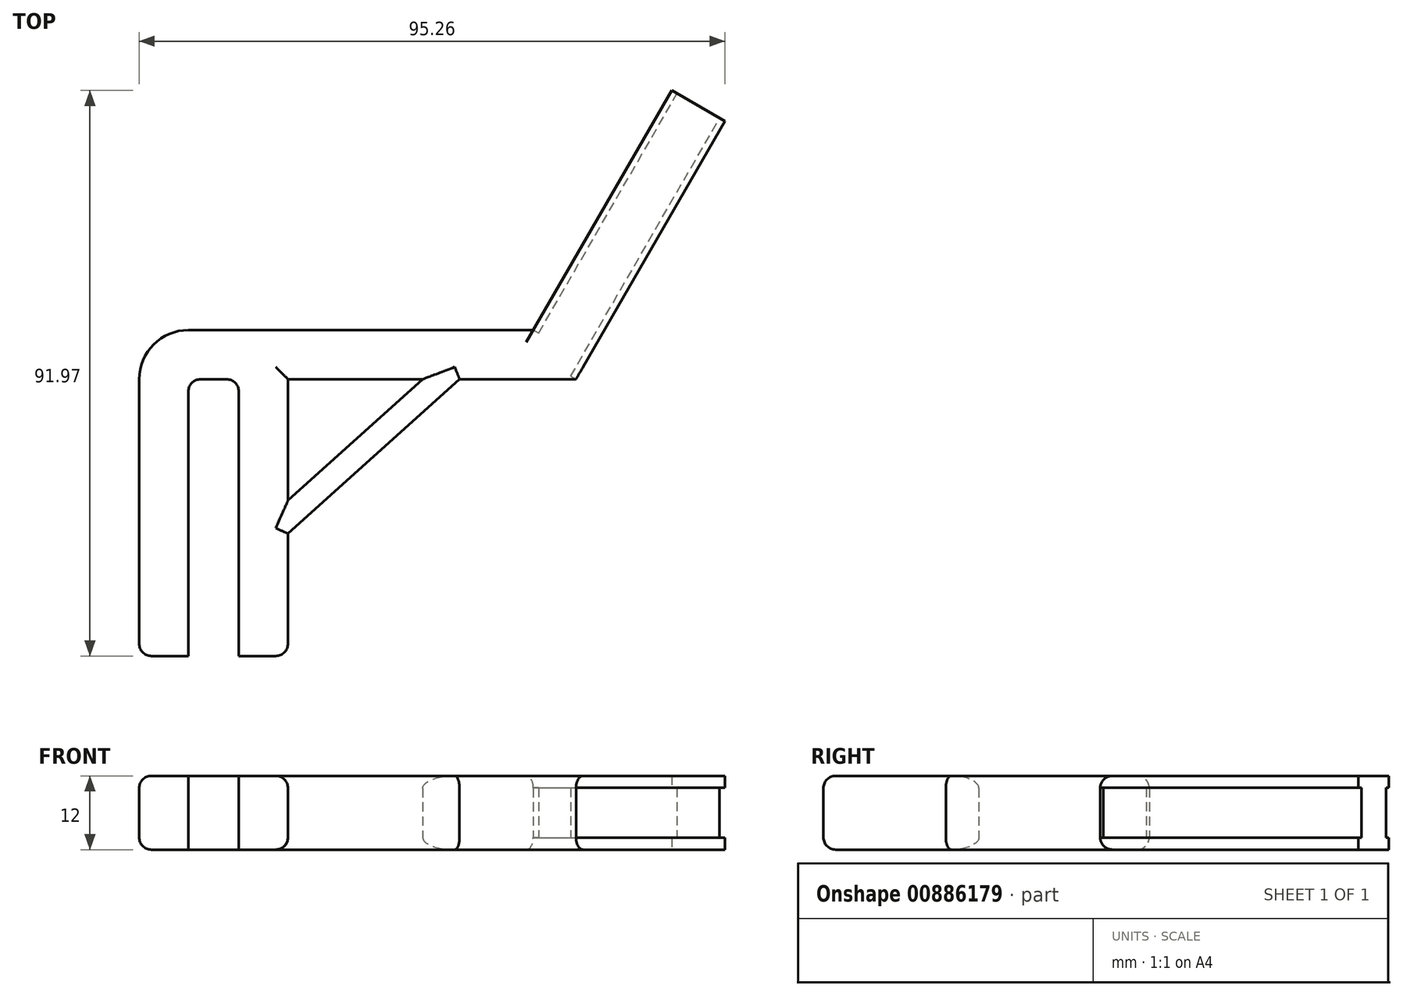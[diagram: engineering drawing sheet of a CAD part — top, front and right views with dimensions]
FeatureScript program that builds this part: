
annotation { "Feature Type Name" : "Feature", "Feature Type Description" : "" }
export const myFeature = defineFeature(function(context is Context, id is Id, definition is map)
    precondition{}
    {
        {
            var Q0;
            Q0=qCreatedBy(makeId("Top.planeOp"),FACE);
            var sketch = newSketch(context, id + "F0", { "sketchPlane" : qUnion([Q0])});
            skLineSegment(sketch, "E0", {"start": v(0, 0) * mm, "end": v(0, 45) * mm});
            skLineSegment(sketch, "E1", {"start": v(24.2, 45) * mm, "end": v(24.2, 25.28) * mm});
            skLineSegment(sketch, "E2", {"start": v(24.2, 0) * mm, "end": v(16.2, 0) * mm});
            skLineSegment(sketch, "E3", {"start": v(16.2, 0) * mm, "end": v(16.2, 43) * mm});
            skLineSegment(sketch, "E4", {"start": v(14.2, 45) * mm, "end": v(10, 45) * mm});
            skLineSegment(sketch, "E5", {"start": v(8, 43) * mm, "end": v(8, 0) * mm});
            skLineSegment(sketch, "E6", {"start": v(8, 0) * mm, "end": v(0, 0) * mm});
            skLineSegment(sketch, "E7", {"start": v(24.2, 45) * mm, "end": v(46.11, 45) * mm});
            skLineSegment(sketch, "E8", {"start": v(71.03, 45) * mm, "end": v(95.26, 86.97) * mm});
            skLineSegment(sketch, "E9", {"start": v(95.26, 86.97) * mm, "end": v(86.6, 91.97) * mm});
            skLineSegment(sketch, "E10", {"start": v(64.1, 53) * mm, "end": v(8, 53) * mm});
            skLineSegment(sketch, "E11", {"start": v(86.6, 91.97) * mm, "end": v(64.1, 53) * mm});
            skLineSegment(sketch, "E12.0.left", {"start": v(24.2, 25.28) * mm, "end": v(46.11, 45) * mm});
            skLineSegment(sketch, "E12.0.right", {"start": v(24.2, 19.9) * mm, "end": v(52.09, 45) * mm});
            skLineSegment(sketch, "E13.trimOffspring", {"start": v(52.09, 45) * mm, "end": v(71.03, 45) * mm});
            skLineSegment(sketch, "E14.trimOffspring", {"start": v(24.2, 19.9) * mm, "end": v(24.2, 0) * mm});
            skPoint(sketch, "E15.visualSharp", {"position": v(0, 53) * mm});
            skPoint(sketch, "E16.visualSharp", {"position": v(16.2, 45) * mm});
            skArc(sketch, "E16.filletArc", {"start": v(16.2, 43) * mm, "mid": v(15.61, 44.41) * mm, "end": v(14.2, 45) * mm});
            skPoint(sketch, "E17.visualSharp", {"position": v(8, 45) * mm});
            skArc(sketch, "E17.filletArc", {"start": v(10, 45) * mm, "mid": v(8.59, 44.41) * mm, "end": v(8, 43) * mm});
            skArc(sketch, "E18.filletArc", {"start": v(8, 53) * mm, "mid": v(2.34, 50.66) * mm, "end": v(0, 45) * mm});
            skSolve(sketch);
        }
        {
            var Q0;
            Q0=makeQuery(id+"F0.imprint","IMPRINT",FACE,{"disambiguationData":[TD([[makeQuery(id+"F0.imprint","IMPRINT",EDGE,{"derivedFrom":sQuery(id+"F0.wireOp",EDGE,"E0")}),-1.0]])]});
            extrude(context, id + "F1", {"entities" : qUnion([Q0]), "depth" : 12 * mm, "offsetDistance" : 25 * mm});
        }
        {
            var Q0;
            Q0=makeQuery(id+"F1.opExtrude","SWEPT_FACE",FACE,{"disambiguationData":[OSD([sQuery(id+"F0.wireOp",EDGE,"0EtChF5o-fKpo-bCFs-vnvd-GfJutQpqdpGe"),sQuery(id+"F0.wireOp",EDGE,"E8")])]});
            var sketch = newSketch(context, id + "F2", { "sketchPlane" : qUnion([Q0])});
            skLineSegment(sketch, "E19.bottom", {"start": v(74.49, 10.05) * mm, "end": v(122.95, 10.05) * mm});
            skLineSegment(sketch, "E19.top", {"start": v(74.49, 1.95) * mm, "end": v(122.95, 1.95) * mm});
            skLineSegment(sketch, "E19.left", {"start": v(74.49, 10.05) * mm, "end": v(74.49, 1.95) * mm});
            skLineSegment(sketch, "E19.right", {"start": v(122.95, 10.05) * mm, "end": v(122.95, 1.95) * mm});
            skSolve(sketch);
        }
        {
            var Q0;
            Q0=makeQuery(id+"F2.imprint","IMPRINT",FACE,{"disambiguationData":[TD([[makeQuery(id+"F2.imprint","IMPRINT",EDGE,{"derivedFrom":sQuery(id+"F2.wireOp",EDGE,"E19.bottom")}),-1.0]])]});
            extrude(context, id + "F3", {"entities" : qUnion([Q0]), "operationType" : NewBodyOperationType.REMOVE, "oppositeDirection" : true, "depth" : 1 * mm, "offsetDistance" : 25 * mm});
        }
        {
            var Q0;
            Q0=makeQuery(id+"F1.opExtrude","SWEPT_FACE",FACE,{"disambiguationData":[OSD([sQuery(id+"F0.wireOp",EDGE,"E11")])]});
            var sketch = newSketch(context, id + "F4", { "sketchPlane" : qUnion([Q0])});
            skLineSegment(sketch, "E20.0", {"start": v(-122.95, 12) * mm, "end": v(-77.95, 12) * mm, "construction": true});
            skLineSegment(sketch, "E20.1", {"start": v(-122.95, 12) * mm, "end": v(-122.95, 0) * mm, "construction": true});
            skLineSegment(sketch, "E20.2", {"start": v(-77.95, 12) * mm, "end": v(-77.95, 0) * mm, "construction": true});
            skLineSegment(sketch, "E20.3", {"start": v(-122.95, 0) * mm, "end": v(-77.95, 0) * mm, "construction": true});
            skLineSegment(sketch, "E21.bottom", {"start": v(-77.95, 1.95) * mm, "end": v(-122.95, 1.95) * mm});
            skLineSegment(sketch, "E21.top", {"start": v(-77.95, 10.05) * mm, "end": v(-122.95, 10.05) * mm});
            skLineSegment(sketch, "E21.left", {"start": v(-77.95, 1.95) * mm, "end": v(-77.95, 10.05) * mm});
            skLineSegment(sketch, "E21.right", {"start": v(-122.95, 1.95) * mm, "end": v(-122.95, 10.05) * mm});
            skPoint(sketch, "E21.middle", {"position": v(-100.45, 6) * mm});
            skPoint(sketch, "E21.middle.positionSnap0", {"position": v(-100.45, 0) * mm});
            skPoint(sketch, "E21.middle.positionSnap1", {"position": v(-122.95, 6) * mm});
            skPoint(sketch, "E21.centerSnap0", {"position": v(-100.45, 0) * mm});
            skPoint(sketch, "E21.centerSnap1", {"position": v(-122.95, 6) * mm});
            skSolve(sketch);
        }
        {
            var Q0;
            Q0=makeQuery(id+"F4.imprint","IMPRINT",FACE,{"disambiguationData":[TD([[makeQuery(id+"F4.imprint","IMPRINT",EDGE,{"derivedFrom":sQuery(id+"F4.wireOp",EDGE,"E21.bottom")}),-1.0]])]});
            extrude(context, id + "F5", {"entities" : qUnion([Q0]), "operationType" : NewBodyOperationType.REMOVE, "oppositeDirection" : true, "depth" : 1 * mm, "offsetDistance" : 25 * mm});
        }
        {
            var Q0;
            Q0=makeQuery(id+"F1.opExtrude","CAP_EDGE",EDGE,{"disambiguationData":[OSD([sQuery(id+"F0.wireOp",EDGE,"E12.0.right")])],"isStart":false});
            var Q1;
            Q1=makeQuery(id+"F1.opExtrude","CAP_EDGE",EDGE,{"disambiguationData":[OSD([sQuery(id+"F0.wireOp",EDGE,"E7")])],"isStart":false});
            var Q2;
            Q2=makeQuery(id+"F1.opExtrude","CAP_EDGE",EDGE,{"disambiguationData":[OSD([sQuery(id+"F0.wireOp",EDGE,"E1")])],"isStart":false});
            var Q3;
            Q3=makeQuery(id+"F1.opExtrude","CAP_EDGE",EDGE,{"disambiguationData":[OSD([sQuery(id+"F0.wireOp",EDGE,"E12.0.left")])],"isStart":false});
            var Q4;
            Q4=makeQuery(id+"F1.opExtrude","CAP_EDGE",EDGE,{"disambiguationData":[OSD([sQuery(id+"F0.wireOp",EDGE,"E13.trimOffspring")])],"isStart":false});
            var Q5;
            Q5=makeQuery(id+"F1.opExtrude","CAP_EDGE",EDGE,{"disambiguationData":[OSD([sQuery(id+"F0.wireOp",EDGE,"E14.trimOffspring")])],"isStart":false});
            var Q6;
            Q6=makeQuery(id+"F1.opExtrude","CAP_EDGE",EDGE,{"disambiguationData":[OSD([sQuery(id+"F0.wireOp",EDGE,"E2")])],"isStart":false});
            var Q7;
            Q7=makeQuery(id+"F1.opExtrude","CAP_EDGE",EDGE,{"disambiguationData":[OSD([sQuery(id+"F0.wireOp",EDGE,"E6")])],"isStart":false});
            var Q8;
            Q8=makeQuery(id+"F1.opExtrude","CAP_EDGE",EDGE,{"disambiguationData":[OSD([sQuery(id+"F0.wireOp",EDGE,"E10")])],"isStart":false});
            var Q9;
            Q9=makeQuery(id+"F1.opExtrude","CAP_EDGE",EDGE,{"disambiguationData":[OSD([sQuery(id+"F0.wireOp",EDGE,"E0")])],"isStart":false});
            var Q10;
            Q10=makeQuery(id+"F1.opExtrude","SWEPT_EDGE",EDGE,{"disambiguationData":[OSD([sQuery(id+"F0.wireOp",EDGE,"E2"),sQuery(id+"F0.wireOp",EDGE,"E14.trimOffspring")])]});
            var Q11;
            Q11=makeQuery(id+"F1.opExtrude","SWEPT_EDGE",EDGE,{"disambiguationData":[OSD([sQuery(id+"F0.wireOp",EDGE,"E0"),sQuery(id+"F0.wireOp",EDGE,"E6")])]});
            var Q12;
            Q12=makeQuery(id+"F1.opExtrude","CAP_EDGE",EDGE,{"disambiguationData":[OSD([sQuery(id+"F0.wireOp",EDGE,"E2")])],"isStart":true});
            var Q13;
            Q13=makeQuery(id+"F1.opExtrude","CAP_EDGE",EDGE,{"disambiguationData":[OSD([sQuery(id+"F0.wireOp",EDGE,"E14.trimOffspring")])],"isStart":true});
            var Q14;
            Q14=makeQuery(id+"F1.opExtrude","CAP_EDGE",EDGE,{"disambiguationData":[OSD([sQuery(id+"F0.wireOp",EDGE,"E12.0.right")])],"isStart":true});
            var Q15;
            Q15=makeQuery(id+"F1.opExtrude","CAP_EDGE",EDGE,{"disambiguationData":[OSD([sQuery(id+"F0.wireOp",EDGE,"E13.trimOffspring")])],"isStart":true});
            var Q16;
            Q16=makeQuery(id+"F1.opExtrude","CAP_EDGE",EDGE,{"disambiguationData":[OSD([sQuery(id+"F0.wireOp",EDGE,"E12.0.left")])],"isStart":true});
            var Q17;
            Q17=makeQuery(id+"F1.opExtrude","CAP_EDGE",EDGE,{"disambiguationData":[OSD([sQuery(id+"F0.wireOp",EDGE,"E7")])],"isStart":true});
            var Q18;
            Q18=makeQuery(id+"F1.opExtrude","CAP_EDGE",EDGE,{"disambiguationData":[OSD([sQuery(id+"F0.wireOp",EDGE,"E1")])],"isStart":true});
            var Q19;
            Q19=makeQuery(id+"F1.opExtrude","CAP_EDGE",EDGE,{"disambiguationData":[OSD([sQuery(id+"F0.wireOp",EDGE,"E0")])],"isStart":true});
            var Q20;
            Q20=makeQuery(id+"F1.opExtrude","CAP_EDGE",EDGE,{"disambiguationData":[OSD([sQuery(id+"F0.wireOp",EDGE,"E10")])],"isStart":true});
            var Q21;
            Q21=makeQuery(id+"F1.opExtrude","CAP_EDGE",EDGE,{"disambiguationData":[OSD([sQuery(id+"F0.wireOp",EDGE,"E6")])],"isStart":true});
            fillet(context, id + "F6", {"entities" : qUnion([Q0, Q1, Q2, Q3, Q4, Q5, Q6, Q7, Q8, Q9, Q10, Q11, Q12, Q13, Q14, Q15, Q16, Q17, Q18, Q19, Q20, Q21]), "radius" : 2 * mm, "tangentPropagation" : true, "allowEdgeOverflow" : false});
        }
    });
